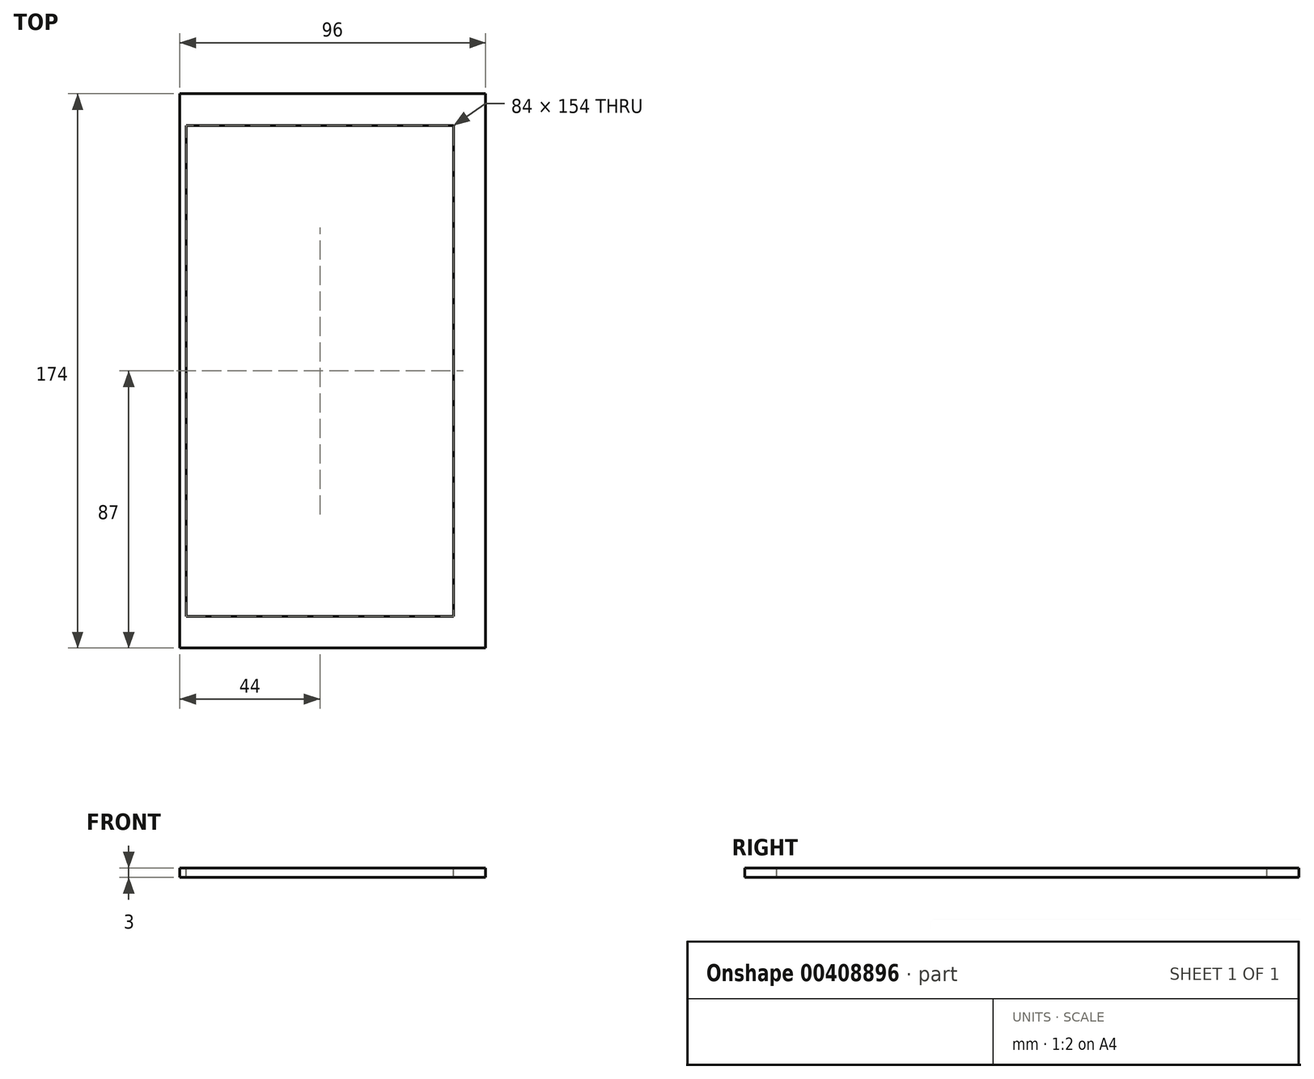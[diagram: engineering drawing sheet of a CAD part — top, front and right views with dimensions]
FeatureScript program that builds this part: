
annotation { "Feature Type Name" : "Feature", "Feature Type Description" : "" }
export const myFeature = defineFeature(function(context is Context, id is Id, definition is map)
    precondition{}
    {
        {
            var Q0;
            Q0=qCreatedBy(makeId("Top.planeOp"),FACE);
            var sketch = newSketch(context, id + "F0", { "sketchPlane" : qUnion([Q0])});
            skLineSegment(sketch, "E0.bottom", {"start": v(-72.05, -133.4) * mm, "end": v(23.95, -133.4) * mm});
            skLineSegment(sketch, "E0.top", {"start": v(-72.05, 40.6) * mm, "end": v(23.95, 40.6) * mm});
            skLineSegment(sketch, "E0.left", {"start": v(-72.05, -133.4) * mm, "end": v(-72.05, 40.6) * mm});
            skLineSegment(sketch, "E0.right", {"start": v(23.95, -133.4) * mm, "end": v(23.95, 40.6) * mm});
            skLineSegment(sketch, "E1.bottom", {"start": v(-70.05, 30.6) * mm, "end": v(13.95, 30.6) * mm});
            skLineSegment(sketch, "E1.top", {"start": v(-70.05, -123.4) * mm, "end": v(13.95, -123.4) * mm});
            skLineSegment(sketch, "E1.left", {"start": v(-70.05, 30.6) * mm, "end": v(-70.05, -123.4) * mm});
            skLineSegment(sketch, "E1.right", {"start": v(13.95, 30.6) * mm, "end": v(13.95, -123.4) * mm});
            skSolve(sketch);
        }
        {
            var Q0;
            Q0 = qSketchRegion(id + "F0", true);
            extrude(context, id + "F1", {"entities" : qUnion([Q0]), "depth" : -3 * mm});
        }
    });
